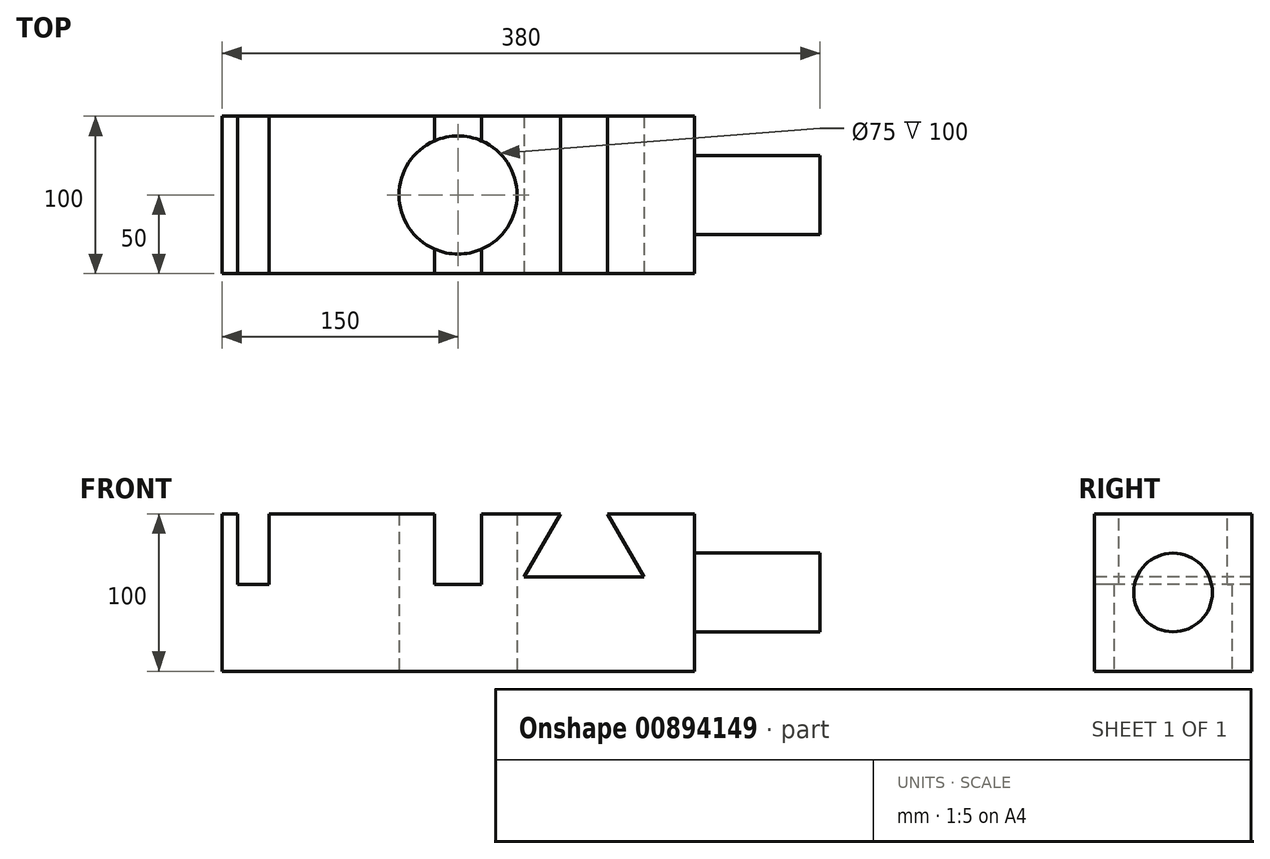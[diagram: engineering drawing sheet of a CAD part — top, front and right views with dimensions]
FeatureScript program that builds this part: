
annotation { "Feature Type Name" : "Feature", "Feature Type Description" : "" }
export const myFeature = defineFeature(function(context is Context, id is Id, definition is map)
    precondition{}
    {
        {
            var Q0;
            Q0=qCreatedBy(makeId("Top.planeOp"),FACE);
            var sketch = newSketch(context, id + "F0", { "sketchPlane" : qUnion([Q0])});
            skLineSegment(sketch, "E0.bottom", {"start": v(150, 50) * mm, "end": v(-150, 50) * mm});
            skLineSegment(sketch, "E0.top", {"start": v(150, -50) * mm, "end": v(-150, -50) * mm});
            skLineSegment(sketch, "E0.left", {"start": v(150, 50) * mm, "end": v(150, -50) * mm});
            skLineSegment(sketch, "E0.right", {"start": v(-150, 50) * mm, "end": v(-150, -50) * mm});
            skPoint(sketch, "E0.middle", {"position": v(0, 0) * mm});
            skCircle(sketch, "E1", {"center": v(0, 0) * mm, "radius": 37.5 * mm});
            skSolve(sketch);
        }
        {
            var Q0;
            Q0=makeQuery(id+"F0.imprint","IMPRINT",FACE,{"disambiguationData":[TD([[makeQuery(id+"F0.imprint","IMPRINT",EDGE,{"derivedFrom":sQuery(id+"F0.wireOp",EDGE,"E0.bottom")}),1.0]])]});
            extrude(context, id + "F1", {"entities" : qUnion([Q0]), "depth" : 100 * mm, "offsetDistance" : 25 * mm});
        }
        {
            var Q0;
            Q0=makeQuery(id+"F1.opExtrude","CAP_FACE",FACE,{"disambiguationData":[OSD([sQuery(id+"F0.wireOp",EDGE,"E0.bottom"),sQuery(id+"F0.wireOp",EDGE,"E0.top"),sQuery(id+"F0.wireOp",EDGE,"E0.left"),sQuery(id+"F0.wireOp",EDGE,"E0.right"),sQuery(id+"F0.wireOp",EDGE,"E1")])],"isStart":false});
            var sketch = newSketch(context, id + "F2", { "sketchPlane" : qUnion([Q0])});
            skLineSegment(sketch, "E2.bottom", {"start": v(-140, 50) * mm, "end": v(-120, 50) * mm});
            skLineSegment(sketch, "E2.top", {"start": v(-140, -50) * mm, "end": v(-120, -50) * mm});
            skLineSegment(sketch, "E2.left", {"start": v(-140, 50) * mm, "end": v(-140, -50) * mm});
            skLineSegment(sketch, "E2.right", {"start": v(-120, 50) * mm, "end": v(-120, -50) * mm});
            skLineSegment(sketch, "E3", {"start": v(-15, 50) * mm, "end": v(-15, -50) * mm});
            skPoint(sketch, "E4", {"position": v(0, 0) * mm});
            skLineSegment(sketch, "E5", {"start": v(15, 50) * mm, "end": v(15, -50) * mm});
            skLineSegment(sketch, "E6", {"start": v(0, 50) * mm, "end": v(0, -50) * mm, "construction": true});
            skSolve(sketch);
        }
        {
            var Q0;
            Q0=makeQuery(id+"F2.imprint","IMPRINT",FACE,{"disambiguationData":[TD([[makeQuery(id+"F2.imprint","IMPRINT",EDGE,{"derivedFrom":sQuery(id+"F2.wireOp",EDGE,"E2.bottom")}),1.0]])]});
            var Q1;
            {var subQ0=sQuery(id+"F2.wireOp",EDGE,"E3");var subQ1=makeQuery(id+"F1.opExtrude","CAP_EDGE",EDGE,{"disambiguationData":[OSD([sQuery(id+"F0.wireOp",EDGE,"E0.top")])],"isStart":false});var subQ2=makeQuery(id+"F2.imprint","INTERSECT",VERTEX,{"derivedFrom":[subQ1,subQ0]});Q1=makeQuery(id+"F2.imprint","IMPRINT",FACE,{"disambiguationData":[TD([[makeQuery(id+"F2.imprint","IMPRINT",EDGE,{"disambiguationData":[TD([[subQ2,1.0]])],"derivedFrom":subQ0}),1.0]])]});}
            var Q2;
            {var subQ0=sQuery(id+"F2.wireOp",EDGE,"E3");var subQ1=makeQuery(id+"F1.opExtrude","CAP_EDGE",EDGE,{"disambiguationData":[OSD([sQuery(id+"F0.wireOp",EDGE,"E0.bottom")])],"isStart":false});var subQ2=makeQuery(id+"F2.imprint","INTERSECT",VERTEX,{"derivedFrom":[subQ1,subQ0]});Q2=makeQuery(id+"F2.imprint","IMPRINT",FACE,{"disambiguationData":[TD([[makeQuery(id+"F2.imprint","IMPRINT",EDGE,{"disambiguationData":[TD([[subQ2,-1.0]])],"derivedFrom":subQ0}),1.0]])]});}
            extrude(context, id + "F3", {"entities" : qUnion([Q0, Q1, Q2]), "operationType" : NewBodyOperationType.REMOVE, "oppositeDirection" : true, "depth" : 45 * mm, "offsetDistance" : 25 * mm});
        }
        {
            var Q0;
            Q0=makeQuery(id+"F1.opExtrude","SWEPT_FACE",FACE,{"disambiguationData":[OSD([sQuery(id+"F0.wireOp",EDGE,"E0.top")])]});
            var sketch = newSketch(context, id + "F4", { "sketchPlane" : qUnion([Q0])});
            skLineSegment(sketch, "E7", {"start": v(65, 100) * mm, "end": v(41.9, 60) * mm});
            skLineSegment(sketch, "E8", {"start": v(41.9, 60) * mm, "end": v(118.1, 60) * mm});
            skLineSegment(sketch, "E9", {"start": v(118.1, 60) * mm, "end": v(95, 100) * mm});
            skLineSegment(sketch, "E10", {"start": v(95, 100) * mm, "end": v(65, 100) * mm});
            skLineSegment(sketch, "E11", {"start": v(80, 60) * mm, "end": v(80, 100) * mm, "construction": true});
            skSolve(sketch);
        }
        {
            var Q0;
            Q0=makeQuery(id+"F4.imprint","IMPRINT",FACE,{"disambiguationData":[TD([[makeQuery(id+"F4.imprint","IMPRINT",EDGE,{"derivedFrom":sQuery(id+"F4.wireOp",EDGE,"E7")}),1.0]])]});
            extrude(context, id + "F5", {"entities" : qUnion([Q0]), "operationType" : NewBodyOperationType.REMOVE, "endBound" : BoundingType.THROUGH_ALL, "oppositeDirection" : true, "depth" : 50 * mm, "offsetDistance" : 25 * mm});
        }
        {
            var Q0;
            Q0=makeQuery(id+"F1.opExtrude","SWEPT_FACE",FACE,{"disambiguationData":[OSD([sQuery(id+"F0.wireOp",EDGE,"E0.left")])]});
            var sketch = newSketch(context, id + "F6", { "sketchPlane" : qUnion([Q0])});
            skCircle(sketch, "E12", {"center": v(0, 50) * mm, "radius": 25 * mm});
            skPoint(sketch, "E12.centerSnap0", {"position": v(-50, 50) * mm});
            skPoint(sketch, "E12.centerSnap1", {"position": v(0, 100) * mm});
            skSolve(sketch);
        }
        {
            var Q0;
            Q0=makeQuery(id+"F6.imprint","IMPRINT",FACE,{"disambiguationData":[TD([[makeQuery(id+"F6.imprint","IMPRINT",EDGE,{"derivedFrom":sQuery(id+"F6.wireOp",EDGE,"E12")}),1.0]])]});
            extrude(context, id + "F7", {"entities" : qUnion([Q0]), "operationType" : NewBodyOperationType.ADD, "depth" : 80 * mm, "offsetDistance" : 25 * mm});
        }
    });
